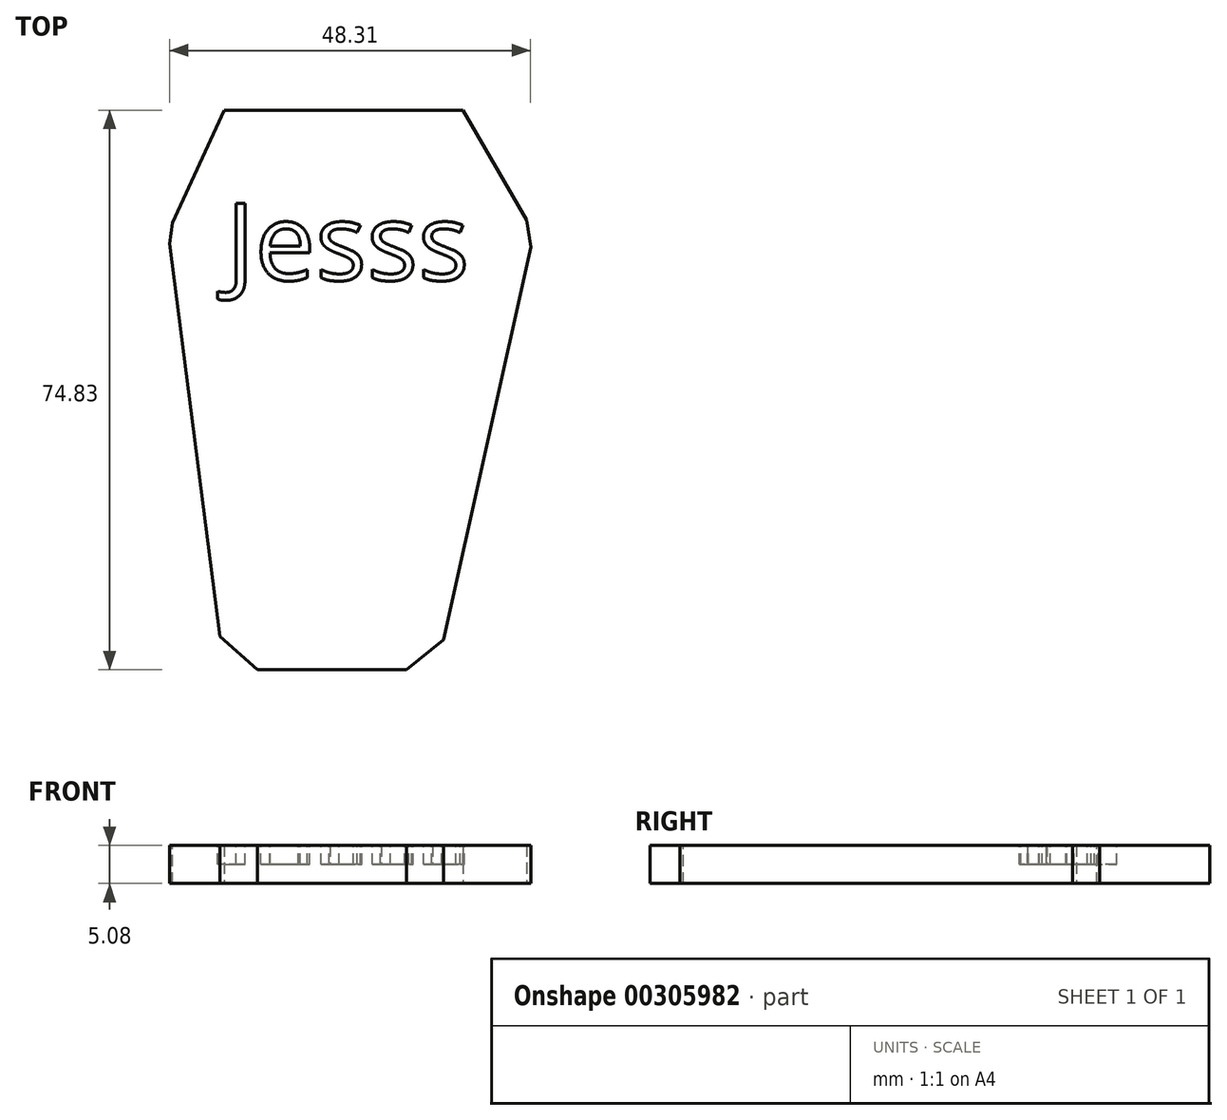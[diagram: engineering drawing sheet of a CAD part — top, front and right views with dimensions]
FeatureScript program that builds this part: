
annotation { "Feature Type Name" : "Feature", "Feature Type Description" : "" }
export const myFeature = defineFeature(function(context is Context, id is Id, definition is map)
    precondition{}
    {
        {
            var Q0;
            Q0=qCreatedBy(makeId("Top.planeOp"),FACE);
            var sketch = newSketch(context, id + "F0", { "sketchPlane" : qUnion([Q0])});
            skLineSegment(sketch, "E0", {"start": v(-60.15, -36.84) * mm, "end": v(-31.66, -36.84) * mm});
            skLineSegment(sketch, "E1", {"start": v(-31.66, -36.84) * mm, "end": v(-18.7, 21.59) * mm});
            skLineSegment(sketch, "E2", {"start": v(-18.7, 21.59) * mm, "end": v(-28.2, 38) * mm});
            skLineSegment(sketch, "E3", {"start": v(-28.2, 38) * mm, "end": v(-60.15, 38) * mm});
            skLineSegment(sketch, "E4", {"start": v(-60.15, 38) * mm, "end": v(-67.63, 21.59) * mm});
            skLineSegment(sketch, "E5", {"start": v(-67.63, 21.59) * mm, "end": v(-60.15, -36.84) * mm});
            skSolve(sketch);
        }
        {
            var Q0;
            Q0 = qSketchRegion(id + "F0", true);
            extrude(context, id + "F1", {"entities" : qUnion([Q0]), "depth" : 5.08 * mm});
        }
        {
            var Q0;
            Q0=makeQuery(id+"F1.opExtrude","SWEPT_EDGE",EDGE,{"disambiguationData":[OSD([sQuery(id+"F0.wireOp",EDGE,"E0"),sQuery(id+"F0.wireOp",EDGE,"E5")])]});
            var Q1;
            Q1=makeQuery(id+"F1.opExtrude","SWEPT_EDGE",EDGE,{"disambiguationData":[OSD([sQuery(id+"F0.wireOp",EDGE,"E0"),sQuery(id+"F0.wireOp",EDGE,"E1")])]});
            chamfer(context, id + "F2", {"entities" : qUnion([Q0, Q1]), "width" : 5.08 * mm, "tangentPropagation" : true});
        }
        {
            var Q0;
            Q0=makeQuery(id+"F1.opExtrude","SWEPT_EDGE",EDGE,{"disambiguationData":[OSD([sQuery(id+"F0.wireOp",EDGE,"E4"),sQuery(id+"F0.wireOp",EDGE,"E5")])]});
            var Q1;
            Q1=makeQuery(id+"F1.opExtrude","SWEPT_EDGE",EDGE,{"disambiguationData":[OSD([sQuery(id+"F0.wireOp",EDGE,"E1"),sQuery(id+"F0.wireOp",EDGE,"E2")])]});
            chamfer(context, id + "F3", {"entities" : qUnion([Q0, Q1]), "width" : 5.08 * mm, "tangentPropagation" : true});
        }
        {
            var Q0;
            Q0=makeQuery(id+"F1.opExtrude","CAP_FACE",FACE,{"disambiguationData":[OSD([sQuery(id+"F0.wireOp",EDGE,"E0"),sQuery(id+"F0.wireOp",EDGE,"E1"),sQuery(id+"F0.wireOp",EDGE,"E2"),sQuery(id+"F0.wireOp",EDGE,"E3"),sQuery(id+"F0.wireOp",EDGE,"E4"),sQuery(id+"F0.wireOp",EDGE,"E5")])],"isStart":false});
            var sketch = newSketch(context, id + "F4", { "sketchPlane" : qUnion([Q0])});
            skText(sketch, "E6", { "text": "Jesss", "fontName": "OpenSans-Regular.ttf"});
            const initialGuessF4  = {"E6": [-0.05986, 0.01525, 1, 0, 0.01036]};
            skSetInitialGuess(sketch, initialGuessF4);
            skSolve(sketch);
        }
        {
            var Q0;
            Q0 = qSketchRegion(id + "F4", true);
            extrude(context, id + "F5", {"entities" : qUnion([Q0]), "operationType" : NewBodyOperationType.REMOVE, "oppositeDirection" : true, "depth" : 2.54 * mm});
        }
    });
